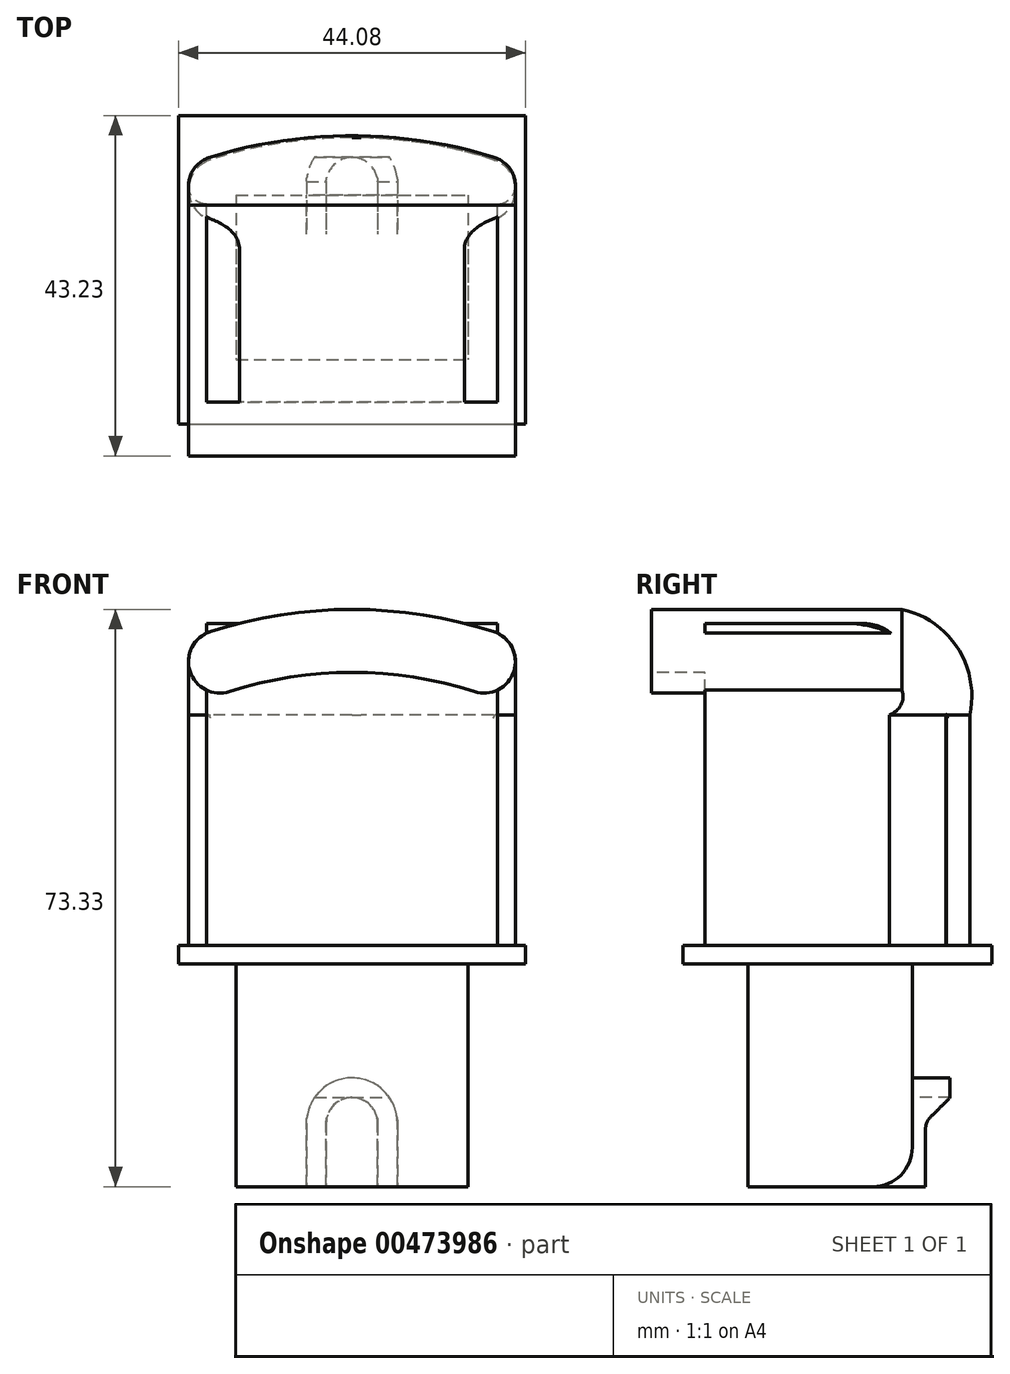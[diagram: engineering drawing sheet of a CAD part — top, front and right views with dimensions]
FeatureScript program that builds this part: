
annotation { "Feature Type Name" : "Feature", "Feature Type Description" : "" }
export const myFeature = defineFeature(function(context is Context, id is Id, definition is map)
    precondition{}
    {
        {
            var Q0;
            Q0=qCreatedBy(makeId("Top.planeOp"),FACE);
            var sketch = newSketch(context, id + "F0", { "sketchPlane" : qUnion([Q0])});
            skLineSegment(sketch, "E0", {"start": v(0, 28.94) * mm, "end": v(0, -26) * mm, "construction": true});
            skLineSegment(sketch, "E1", {"start": v(-27.87, 0) * mm, "end": v(24.49, 0) * mm, "construction": true});
            skLineSegment(sketch, "E2.bottom", {"start": v(-22.04, 19.6) * mm, "end": v(22.04, 19.6) * mm});
            skLineSegment(sketch, "E2.top", {"start": v(-22.04, -19.6) * mm, "end": v(22.04, -19.6) * mm});
            skLineSegment(sketch, "E2.left", {"start": v(-22.04, 19.6) * mm, "end": v(-22.04, -19.6) * mm});
            skLineSegment(sketch, "E2.right", {"start": v(22.04, 19.6) * mm, "end": v(22.04, -19.6) * mm});
            skSolve(sketch);
        }
        {
            var Q0;
            Q0=qCreatedBy(makeId("Top.planeOp"),FACE);
            var sketch = newSketch(context, id + "F1", { "sketchPlane" : qUnion([Q0])});
            skLineSegment(sketch, "E3.top", {"start": v(-18.5, -16.8) * mm, "end": v(18.5, -16.8) * mm});
            skLineSegment(sketch, "E3.left", {"start": v(-18.5, 13.83) * mm, "end": v(-18.5, -16.8) * mm});
            skLineSegment(sketch, "E3.right", {"start": v(18.5, 13.83) * mm, "end": v(18.5, -16.8) * mm});
            skArc(sketch, "E4", {"start": v(-18.5, 13.83) * mm, "mid": v(0, 16.8) * mm, "end": v(18.5, 13.83) * mm});
            skPoint(sketch, "E5", {"position": v(0, -16.8) * mm});
            skPoint(sketch, "E6", {"position": v(0, 16.8) * mm});
            skSolve(sketch);
        }
        {
            var Q0;
            Q0=qCreatedBy(makeId("Top.planeOp"),FACE);
            var sketch = newSketch(context, id + "F2", { "sketchPlane" : qUnion([Q0])});
            skLineSegment(sketch, "E7.bottom", {"start": v(-14.72, 9.51) * mm, "end": v(14.72, 9.51) * mm});
            skLineSegment(sketch, "E7.top", {"start": v(-14.72, -11.4) * mm, "end": v(14.72, -11.4) * mm});
            skLineSegment(sketch, "E7.left", {"start": v(-14.72, 9.51) * mm, "end": v(-14.72, -11.4) * mm});
            skLineSegment(sketch, "E7.right", {"start": v(14.72, 9.51) * mm, "end": v(14.72, -11.4) * mm});
            skSolve(sketch);
        }
        {
            var Q0;
            Q0 = qSketchRegion(id + "F2", true);
            extrude(context, id + "F3", {"entities" : qUnion([Q0]), "depth" : -28.27 * mm});
        }
        {
            var Q0;
            Q0=makeQuery(id+"F3.opExtrude","CAP_EDGE",EDGE,{"disambiguationData":[OSD([sQuery(id+"F2.wireOp",EDGE,"E7.bottom")])],"isStart":false});
            fillet(context, id + "F4", {"entities" : qUnion([Q0]), "radius" : 5 * mm, "tangentPropagation" : true, "allowEdgeOverflow" : false});
        }
        {
            var Q0;
            Q0=makeQuery(id+"F3.opExtrude","SWEPT_FACE",FACE,{"disambiguationData":[OSD([sQuery(id+"F2.wireOp",EDGE,"E7.top")])]});
            var sketch = newSketch(context, id + "F5", { "sketchPlane" : qUnion([Q0])});
            skLineSegment(sketch, "E8.bottom", {"start": v(-5.77, -28.27) * mm, "end": v(-3.28, -28.27) * mm});
            skLineSegment(sketch, "E8.left", {"start": v(-5.77, -28.27) * mm, "end": v(-5.78, -20.23) * mm});
            skLineSegment(sketch, "E8.right", {"start": v(5.77, -28.27) * mm, "end": v(5.78, -20.23) * mm});
            skArc(sketch, "E9", {"start": v(-5.78, -20.23) * mm, "mid": v(0, -14.45) * mm, "end": v(5.78, -20.23) * mm});
            skLineSegment(sketch, "E10", {"start": v(-3.28, -20.23) * mm, "end": v(-3.28, -28.27) * mm});
            skLineSegment(sketch, "E11.MirrorCS", {"start": v(3.28, -20.23) * mm, "end": v(3.28, -28.27) * mm});
            skArc(sketch, "E12", {"start": v(-3.28, -20.23) * mm, "mid": v(0, -16.95) * mm, "end": v(3.28, -20.23) * mm});
            skLineSegment(sketch, "E13.trimOffspring", {"start": v(3.28, -28.27) * mm, "end": v(5.77, -28.27) * mm});
            skSolve(sketch);
        }
        {
            var Q0;
            Q0 = qSketchRegion(id + "F5", true);
            extrude(context, id + "F6", {"entities" : qUnion([Q0]), "operationType" : NewBodyOperationType.ADD, "oppositeDirection" : true, "depth" : 25.7 * mm});
        }
        {
            var Q0;
            Q0=qCreatedBy(makeId("Right.planeOp"),FACE);
            var sketch = newSketch(context, id + "F7", { "sketchPlane" : qUnion([Q0])});
            skLineSegment(sketch, "E14", {"start": v(14.3, -16.95) * mm, "end": v(11.78, -19.47) * mm});
            skLineSegment(sketch, "E15", {"start": v(11.2, -20.89) * mm, "end": v(11.2, -28.27) * mm});
            skPoint(sketch, "E16.visualSharp", {"position": v(11.2, -20.06) * mm});
            skArc(sketch, "E16.filletArc", {"start": v(11.78, -19.47) * mm, "mid": v(11.35, -20.12) * mm, "end": v(11.2, -20.89) * mm});
            skLineSegment(sketch, "E17", {"start": v(14.3, -16.95) * mm, "end": v(14.3, -28.27) * mm});
            skLineSegment(sketch, "E18", {"start": v(14.3, -28.27) * mm, "end": v(11.2, -28.27) * mm});
            skSolve(sketch);
        }
        {
            var Q0;
            Q0 = qSketchRegion(id + "F7", true);
            extrude(context, id + "F8", {"entities" : qUnion([Q0]), "operationType" : NewBodyOperationType.REMOVE, "endBound" : BoundingType.SYMMETRIC, "oppositeDirection" : true, "depth" : 25 * mm});
        }
        {
            var Q0;
            Q0=makeQuery(id+"F0.imprint","IMPRINT",FACE,{"disambiguationData":[TD([[makeQuery(id+"F0.imprint","IMPRINT",EDGE,{"derivedFrom":sQuery(id+"F0.wireOp",EDGE,"E2.bottom")}),-1.0]])]});
            extrude(context, id + "F9", {"entities" : qUnion([Q0]), "operationType" : NewBodyOperationType.ADD, "depth" : 2.4 * mm});
        }
        {
            var Q0;
            Q0 = qSketchRegion(id + "F1", true);
            extrude(context, id + "F10", {"entities" : qUnion([Q0]), "operationType" : NewBodyOperationType.ADD, "depth" : 43.3 * mm});
        }
        {
            var Q0;
            Q0=makeQuery(id+"F10.opExtrude","CAP_EDGE",EDGE,{"disambiguationData":[OSD([sQuery(id+"F1.wireOp",EDGE,"E4")])],"isStart":false});
            fillet(context, id + "F11", {"entities" : qUnion([Q0]), "radius" : 12 * mm, "tangentPropagation" : true, "allowEdgeOverflow" : false});
        }
        {
            var Q0;
            Q0=makeQuery(id+"F9.opExtrude","CAP_FACE",FACE,{"disambiguationData":[OSD([sQuery(id+"F0.wireOp",EDGE,"E2.bottom"),sQuery(id+"F0.wireOp",EDGE,"E2.top"),sQuery(id+"F0.wireOp",EDGE,"E2.left"),sQuery(id+"F0.wireOp",EDGE,"E2.right")])],"isStart":false});
            var sketch = newSketch(context, id + "F12", { "sketchPlane" : qUnion([Q0])});
            skLineSegment(sketch, "E19.bottom", {"start": v(0, 18.14) * mm, "end": v(1.18, 18.14) * mm});
            skLineSegment(sketch, "E19.top", {"start": v(0, 15.1) * mm, "end": v(1.18, 15.1) * mm});
            skLineSegment(sketch, "E19.left", {"start": v(0, 18.14) * mm, "end": v(0, 15.1) * mm});
            skLineSegment(sketch, "E19.right", {"start": v(1.18, 18.14) * mm, "end": v(1.18, 15.1) * mm});
            skSolve(sketch);
        }
        {
            var Q0;
            Q0 = qSketchRegion(id + "F12", true);
            extrude(context, id + "F13", {"entities" : qUnion([Q0]), "operationType" : NewBodyOperationType.REMOVE, "endBound" : BoundingType.THROUGH_ALL, "depth" : 25 * mm});
        }
        {
            var Q0;
            Q0=qCreatedBy(makeId("Right.planeOp"),FACE);
            var sketch = newSketch(context, id + "F14", { "sketchPlane" : qUnion([Q0])});
            skLineSegment(sketch, "E20", {"start": v(16.8, 2.4) * mm, "end": v(16.8, 34.06) * mm});
            skLineSegment(sketch, "E21", {"start": v(5.8, 45.06) * mm, "end": v(-26.03, 45.06) * mm});
            skPoint(sketch, "E22.visualSharp", {"position": v(16.8, 45.06) * mm});
            skArc(sketch, "E22.filletArc", {"start": v(16.8, 34.06) * mm, "mid": v(13.59, 41.84) * mm, "end": v(5.8, 45.06) * mm});
            skSolve(sketch);
        }
        {
            var Q0;
            Q0=qCreatedBy(makeId("Top.planeOp"),FACE);
            var sketch = newSketch(context, id + "F15", { "sketchPlane" : qUnion([Q0])});
            skArc(sketch, "E23.0", {"start": v(-17.98, 14) * mm, "mid": v(-9.1, 16.1) * mm, "end": v(0, 16.8) * mm});
            skPoint(sketch, "E24.newPointA", {"position": v(-18.5, 13.83) * mm});
            skArc(sketch, "E25.0", {"start": v(-15.53, 6.38) * mm, "mid": v(-7.86, 8.2) * mm, "end": v(0, 8.8) * mm});
            skArc(sketch, "E26", {"start": v(-17.98, 14) * mm, "mid": v(-20.57, 8.96) * mm, "end": v(-15.53, 6.38) * mm});
            skArc(sketch, "E27.MirrorCS", {"start": v(17.98, 14) * mm, "mid": v(9.1, 16.1) * mm, "end": v(0, 16.8) * mm});
            skArc(sketch, "E28.MirrorCS", {"start": v(17.98, 14) * mm, "mid": v(20.57, 8.96) * mm, "end": v(15.53, 6.38) * mm});
            skArc(sketch, "E29.MirrorCS", {"start": v(15.53, 6.38) * mm, "mid": v(7.86, 8.2) * mm, "end": v(0, 8.8) * mm});
            skSolve(sketch);
        }
        {
            var Q0;
            Q0 = qSketchRegion(id + "F15", true);
            var Q1;
            Q1 = qConstructionFilter(qBodyType(qCreatedBy(id + "F14" ,EDGE), BodyType.WIRE), ConstructionObject.NO);
            sweep(context, id + "F16", {"operationType" : NewBodyOperationType.ADD, "profiles" : qUnion([Q0]), "path" : qUnion([Q1])});
        }
    });
